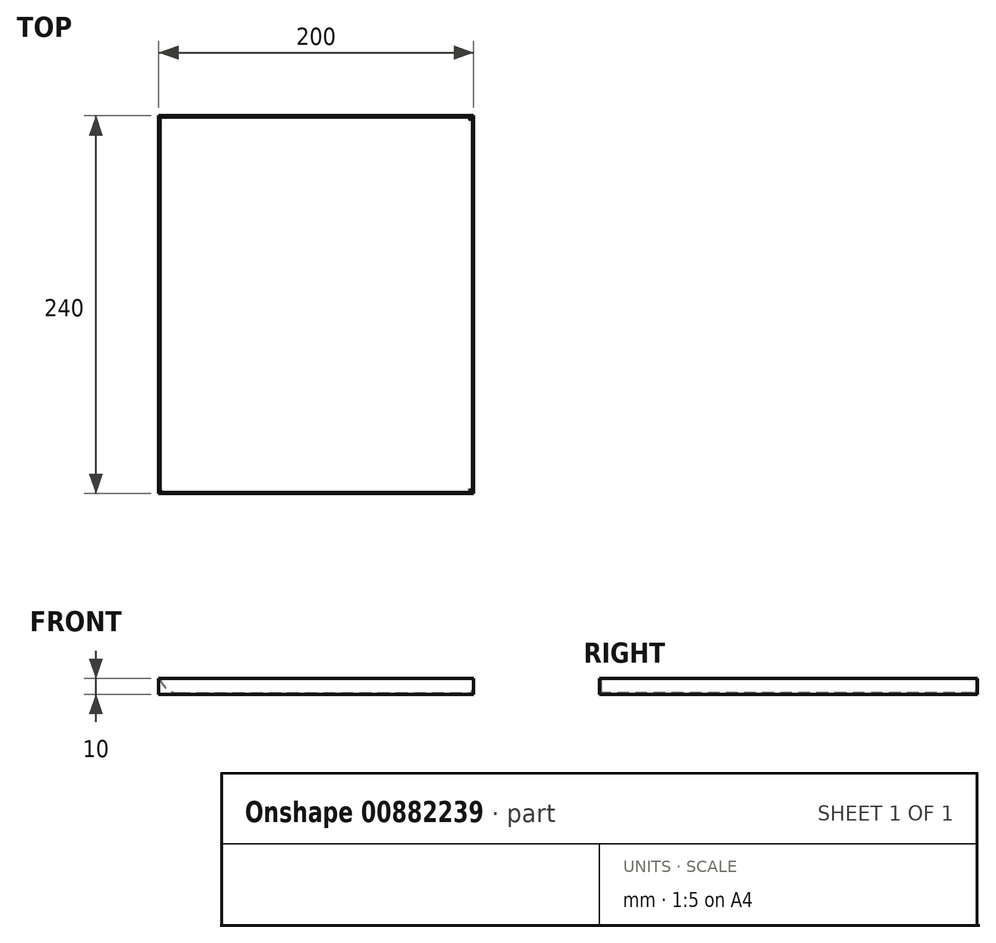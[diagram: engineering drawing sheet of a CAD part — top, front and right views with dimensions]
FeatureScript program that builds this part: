
annotation { "Feature Type Name" : "Feature", "Feature Type Description" : "" }
export const myFeature = defineFeature(function(context is Context, id is Id, definition is map)
    precondition{}
    {
        {
            var Q0;
            Q0=qCreatedBy(makeId("Top.planeOp"),FACE);
            var sketch = newSketch(context, id + "F0", { "sketchPlane" : qUnion([Q0])});
            skLineSegment(sketch, "E0.bottom", {"start": v(-90.65, -111.38) * mm, "end": v(109.35, -111.38) * mm});
            skLineSegment(sketch, "E0.top", {"start": v(-90.65, 128.62) * mm, "end": v(109.35, 128.62) * mm});
            skLineSegment(sketch, "E0.left", {"start": v(-90.65, -111.38) * mm, "end": v(-90.65, 128.62) * mm});
            skLineSegment(sketch, "E0.right", {"start": v(109.35, -111.38) * mm, "end": v(109.35, 128.62) * mm});
            skSolve(sketch);
        }
        {
            var Q0;
            Q0 = qSketchRegion(id + "F0", true);
            var Q1;
            Q1=makeQuery(id+"F0.imprint","IMPRINT",FACE,{"disambiguationData":[TD([[makeQuery(id+"F0.imprint","IMPRINT",EDGE,{"derivedFrom":sQuery(id+"F0.wireOp",EDGE,"E0.bottom")}),1.0]])]});
            extrude(context, id + "F1", {"entities" : qUnion([Q0, Q1]), "depth" : 10 * mm, "offsetDistance" : 25 * mm});
        }
        {
            var Q0;
            Q0=makeQuery(id+"F1.opExtrude","CAP_FACE",FACE,{"disambiguationData":[OSD([sQuery(id+"F0.wireOp",EDGE,"E0.bottom"),sQuery(id+"F0.wireOp",EDGE,"E0.top"),sQuery(id+"F0.wireOp",EDGE,"E0.left"),sQuery(id+"F0.wireOp",EDGE,"E0.right")])],"isStart":false});
            shell(context, id + "F2", {"entities" : qUnion([Q0]), "thickness" : 0.8 * mm});
        }
        {
            var Q0;
            {var subQ0=sQuery(id+"F0.wireOp",EDGE,"E0.left");Q0=makeQuery(id+"F2.opShell","OFFSET_EDGE",EDGE,{"disambiguationData":[OSD([subQ0]),TDD([makeQuery(id+"F1.opExtrude","CAP_EDGE",EDGE,{"disambiguationData":[OSD([subQ0])],"isStart":true})])]});}
            fillet(context, id + "F3", {"entities" : qUnion([Q0]), "radius" : 12 * mm, "tangentPropagation" : true, "allowEdgeOverflow" : false});
        }
        {
            var Q0;
            {var subQ0=sQuery(id+"F0.wireOp",EDGE,"E0.top");Q0=makeQuery(id+"F2.opShell","OFFSET_EDGE",EDGE,{"disambiguationData":[OSD([subQ0]),TDD([makeQuery(id+"F1.opExtrude","CAP_EDGE",EDGE,{"disambiguationData":[OSD([subQ0])],"isStart":true})])]});}
            var Q1;
            {var subQ0=sQuery(id+"F0.wireOp",EDGE,"E0.bottom");Q1=makeQuery(id+"F2.opShell","OFFSET_EDGE",EDGE,{"disambiguationData":[OSD([subQ0]),TDD([makeQuery(id+"F1.opExtrude","CAP_EDGE",EDGE,{"disambiguationData":[OSD([subQ0])],"isStart":true})])]});}
            var Q2;
            {var subQ0=sQuery(id+"F0.wireOp",EDGE,"E0.right");Q2=makeQuery(id+"F2.opShell","OFFSET_EDGE",EDGE,{"disambiguationData":[OSD([subQ0]),TDD([makeQuery(id+"F1.opExtrude","CAP_EDGE",EDGE,{"disambiguationData":[OSD([subQ0])],"isStart":true})])]});}
            fillet(context, id + "F4", {"entities" : qUnion([Q0, Q1, Q2]), "radius" : 2 * mm, "tangentPropagation" : true, "allowEdgeOverflow" : false});
        }
    });
